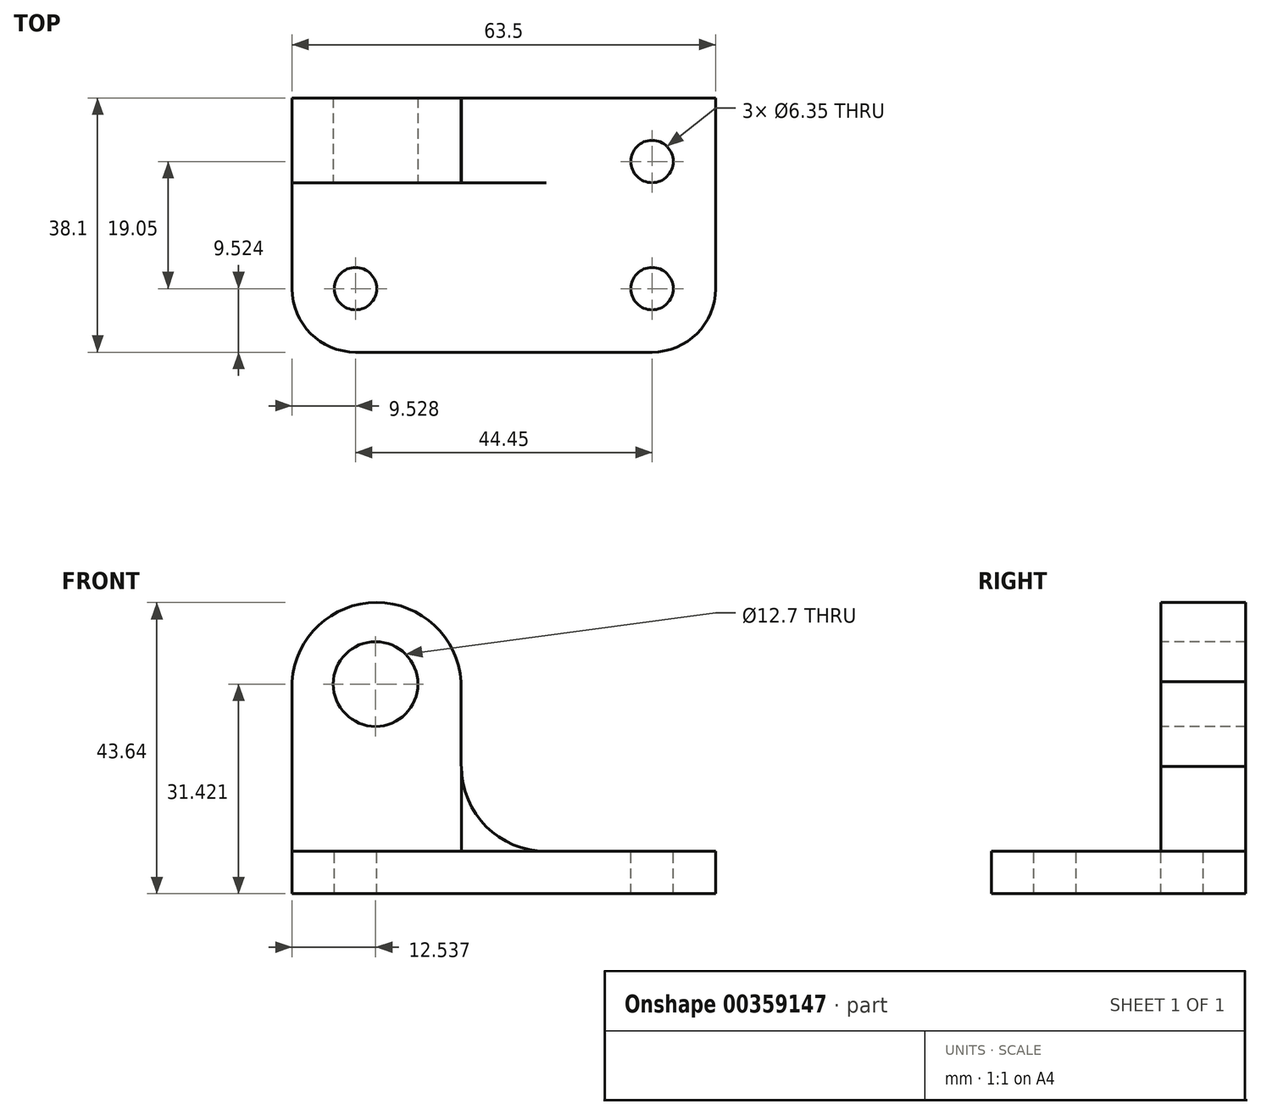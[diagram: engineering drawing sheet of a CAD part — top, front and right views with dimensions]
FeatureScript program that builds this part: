
annotation { "Feature Type Name" : "Feature", "Feature Type Description" : "" }
export const myFeature = defineFeature(function(context is Context, id is Id, definition is map)
    precondition{}
    {
        {
            var Q0;
            Q0=qCreatedBy(makeId("Top.planeOp"),FACE);
            var sketch = newSketch(context, id + "F0", { "sketchPlane" : qUnion([Q0])});
            skLineSegment(sketch, "E0", {"start": v(-40.1, 20.93) * mm, "end": v(23.4, 20.93) * mm});
            skLineSegment(sketch, "E1", {"start": v(23.4, 20.93) * mm, "end": v(23.4, -17.17) * mm});
            skLineSegment(sketch, "E2", {"start": v(23.4, -17.17) * mm, "end": v(-40.1, -17.17) * mm});
            skLineSegment(sketch, "E3", {"start": v(-40.1, -17.17) * mm, "end": v(-40.1, 20.93) * mm});
            skSolve(sketch);
        }
        {
            var Q0;
            Q0 = qSketchRegion(id + "F0", true);
            extrude(context, id + "F1", {"entities" : qUnion([Q0]), "depth" : 6.35 * mm});
        }
        {
            var Q0;
            Q0=makeQuery(id+"F1.opExtrude","CAP_FACE",FACE,{"disambiguationData":[OSD([sQuery(id+"F0.wireOp",EDGE,"E0"),sQuery(id+"F0.wireOp",EDGE,"E1"),sQuery(id+"F0.wireOp",EDGE,"E2"),sQuery(id+"F0.wireOp",EDGE,"E3")])],"isStart":false});
            var sketch = newSketch(context, id + "F2", { "sketchPlane" : qUnion([Q0])});
            skCircle(sketch, "E4", {"center": v(-30.58, -7.65) * mm, "radius": 3.18 * mm});
            skCircle(sketch, "E5", {"center": v(13.87, -7.65) * mm, "radius": 3.18 * mm});
            skCircle(sketch, "E6", {"center": v(13.87, 11.4) * mm, "radius": 3.18 * mm});
            skArc(sketch, "E7", {"start": v(-40.1, -7.65) * mm, "mid": v(-37.31, -14.38) * mm, "end": v(-30.58, -17.17) * mm});
            skArc(sketch, "E8", {"start": v(13.87, -17.17) * mm, "mid": v(20.6, -14.38) * mm, "end": v(23.4, -7.65) * mm});
            skSolve(sketch);
        }
        {
            var Q0;
            Q0 = qSketchRegion(id + "F2", true);
            var Q1;
            {var subQ0=sQuery(id+"F2.wireOp",EDGE,"E7");Q1=makeQuery(id+"F2.imprint","IMPRINT",FACE,{"disambiguationData":[TD([[makeQuery(id+"F2.imprint","IMPRINT",EDGE,{"derivedFrom":subQ0}),-1.0]])]});}
            var Q2;
            {var subQ0=sQuery(id+"F2.wireOp",EDGE,"E8");Q2=makeQuery(id+"F2.imprint","IMPRINT",FACE,{"disambiguationData":[TD([[makeQuery(id+"F2.imprint","IMPRINT",EDGE,{"derivedFrom":subQ0}),-1.0]])]});}
            extrude(context, id + "F3", {"entities" : qUnion([Q0, Q1, Q2]), "operationType" : NewBodyOperationType.REMOVE, "oppositeDirection" : true, "depth" : 6.35 * mm});
        }
        {
            var Q0;
            Q0=makeQuery(id+"F1.opExtrude","CAP_FACE",FACE,{"disambiguationData":[OSD([sQuery(id+"F0.wireOp",EDGE,"E0"),sQuery(id+"F0.wireOp",EDGE,"E1"),sQuery(id+"F0.wireOp",EDGE,"E2"),sQuery(id+"F0.wireOp",EDGE,"E3")])],"isStart":false});
            var sketch = newSketch(context, id + "F4", { "sketchPlane" : qUnion([Q0])});
            skLineSegment(sketch, "E9.bottom", {"start": v(-40.1, 20.93) * mm, "end": v(-2, 20.93) * mm});
            skLineSegment(sketch, "E9.top", {"start": v(-40.1, 8.23) * mm, "end": v(-2, 8.23) * mm});
            skLineSegment(sketch, "E9.left", {"start": v(-40.1, 20.93) * mm, "end": v(-40.1, 8.23) * mm});
            skLineSegment(sketch, "E9.right", {"start": v(-2, 20.93) * mm, "end": v(-2, 8.23) * mm});
            skSolve(sketch);
        }
        {
            var Q0;
            Q0 = qSketchRegion(id + "F4", true);
            extrude(context, id + "F5", {"entities" : qUnion([Q0]), "operationType" : NewBodyOperationType.ADD, "depth" : 38.1 * mm});
        }
        {
            var Q0;
            Q0=makeQuery(id+"F5.opExtrude","SWEPT_FACE",FACE,{"disambiguationData":[OSD([sQuery(id+"F4.wireOp",EDGE,"E9.top")])]});
            var sketch = newSketch(context, id + "F6", { "sketchPlane" : qUnion([Q0])});
            skLineSegment(sketch, "E10", {"start": v(-14.7, 19.05) * mm, "end": v(-14.7, 6.35) * mm});
            skArc(sketch, "E11", {"start": v(-14.7, 19.05) * mm, "mid": v(-10.99, 10.07) * mm, "end": v(-2, 6.35) * mm});
            skLineSegment(sketch, "E12", {"start": v(-40.1, 31.75) * mm, "end": v(-2, 31.75) * mm});
            skCircle(sketch, "E13", {"center": v(-27.57, 31.42) * mm, "radius": 6.35 * mm});
            skLineSegment(sketch, "E14", {"start": v(-14.78, 44.45) * mm, "end": v(-14.7, 6.35) * mm});
            skArc(sketch, "E15", {"start": v(-14.76, 31.75) * mm, "mid": v(-27.43, 43.64) * mm, "end": v(-40.1, 31.75) * mm});
            skSolve(sketch);
        }
        {
            var Q0;
            {var subQ0=sQuery(id+"F6.wireOp",EDGE,"E13");var subQ1=sQuery(id+"F6.wireOp",EDGE,"E12");var subQ2=makeQuery(id+"F6.imprint","INTERSECT",VERTEX,{"disambiguationData":[OD(0.0)],"derivedFrom":[subQ1,subQ0]});Q0=makeQuery(id+"F6.imprint","IMPRINT",FACE,{"disambiguationData":[TD([[makeQuery(id+"F6.imprint","IMPRINT",EDGE,{"disambiguationData":[TD([[subQ2,-1.0]])],"derivedFrom":subQ1}),1.0]])]});}
            var Q1;
            {var subQ0=sQuery(id+"F6.wireOp",EDGE,"E13");var subQ1=sQuery(id+"F6.wireOp",EDGE,"E12");var subQ2=makeQuery(id+"F6.imprint","INTERSECT",VERTEX,{"disambiguationData":[OD(0.0)],"derivedFrom":[subQ1,subQ0]});Q1=makeQuery(id+"F6.imprint","IMPRINT",FACE,{"disambiguationData":[TD([[makeQuery(id+"F6.imprint","IMPRINT",EDGE,{"disambiguationData":[TD([[subQ2,-1.0]])],"derivedFrom":subQ1}),-1.0]])]});}
            var Q2;
            {var subQ1=sQuery(id+"F6.wireOp",EDGE,"E10");Q2=makeQuery(id+"F6.imprint","IMPRINT",FACE,{"disambiguationData":[TD([[makeQuery(id+"F6.imprint","IMPRINT",EDGE,{"derivedFrom":subQ1}),-1.0]])]});}
            var Q3;
            {var subQ1=sQuery(id+"F4.wireOp",EDGE,"E9.top");var subQ4=sQuery(id+"F6.wireOp",EDGE,"E14");var subQ6=makeQuery(id+"F5.opExtrude","CAP_EDGE",EDGE,{"disambiguationData":[OSD([subQ1])],"isStart":false});var subQ7=makeQuery(id+"F6.imprint","INTERSECT",VERTEX,{"derivedFrom":[subQ6,subQ4]});Q3=makeQuery(id+"F6.imprint","IMPRINT",FACE,{"disambiguationData":[TD([[makeQuery(id+"F6.imprint","IMPRINT",EDGE,{"disambiguationData":[TD([[subQ7,-1.0]])],"derivedFrom":subQ4}),1.0]])]});}
            var Q4;
            {var subQ4=sQuery(id+"F6.wireOp",EDGE,"E15");Q4=makeQuery(id+"F6.imprint","IMPRINT",FACE,{"disambiguationData":[TD([[makeQuery(id+"F6.imprint","IMPRINT",EDGE,{"derivedFrom":subQ4}),-1.0]])]});}
            extrude(context, id + "F7", {"entities" : qUnion([Q0, Q1, Q2, Q3, Q4]), "operationType" : NewBodyOperationType.REMOVE, "oppositeDirection" : true, "depth" : 25.4 * mm});
        }
    });
